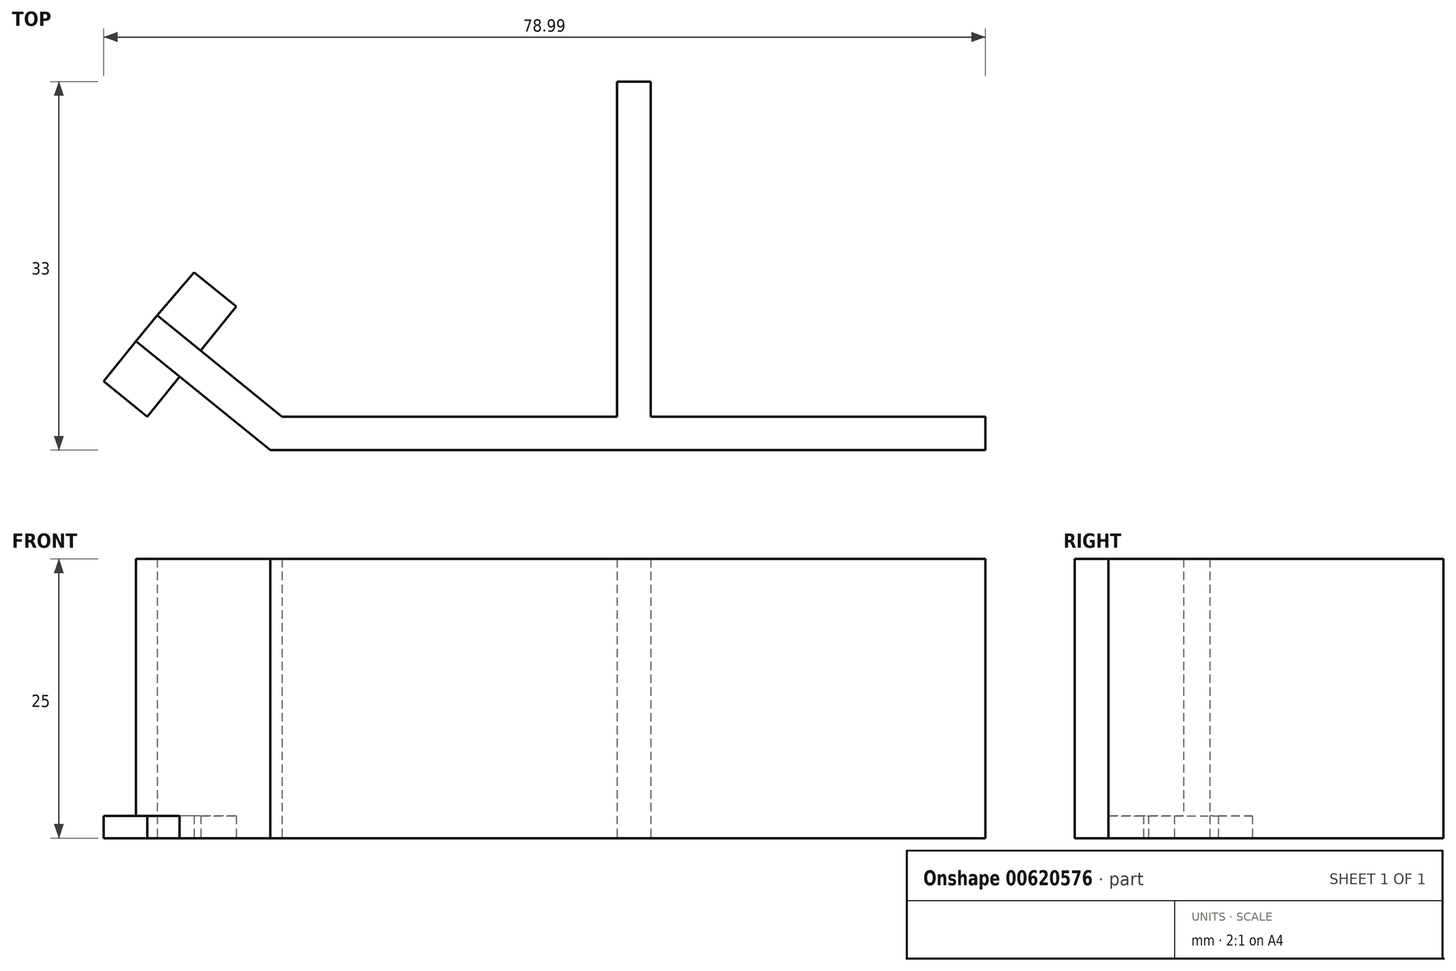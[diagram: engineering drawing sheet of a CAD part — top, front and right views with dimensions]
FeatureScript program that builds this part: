
annotation { "Feature Type Name" : "Feature", "Feature Type Description" : "" }
export const myFeature = defineFeature(function(context is Context, id is Id, definition is map)
    precondition{}
    {
        {
            var Q0;
            Q0=qCreatedBy(makeId("Top.planeOp"),FACE);
            var sketch = newSketch(context, id + "F0", { "sketchPlane" : qUnion([Q0])});
            skLineSegment(sketch, "E0", {"start": v(0, 0) * mm, "end": v(-30, 0) * mm});
            skLineSegment(sketch, "E1", {"start": v(-30, 0) * mm, "end": v(-41.2, 9.08) * mm});
            skLineSegment(sketch, "E2", {"start": v(0, 0) * mm, "end": v(0, 30) * mm});
            skLineSegment(sketch, "E3", {"start": v(3, 30) * mm, "end": v(0, 30) * mm});
            skLineSegment(sketch, "E4", {"start": v(3, 30) * mm, "end": v(3, -3) * mm});
            skLineSegment(sketch, "E5.0", {"start": v(-31.06, -3) * mm, "end": v(-43.08, 6.75) * mm});
            skLineSegment(sketch, "E5.1", {"start": v(3, -3) * mm, "end": v(-31.06, -3) * mm});
            skLineSegment(sketch, "E6", {"start": v(-43.08, 6.75) * mm, "end": v(-41.2, 9.08) * mm});
            skPoint(sketch, "E7.orphan", {"position": v(3, 0) * mm});
            skLineSegment(sketch, "E8", {"start": v(3, -3) * mm, "end": v(33, -3) * mm});
            skLineSegment(sketch, "E9", {"start": v(33, -3) * mm, "end": v(33, 0) * mm});
            skLineSegment(sketch, "E10", {"start": v(33, 0) * mm, "end": v(3, 0) * mm});
            skSolve(sketch);
        }
        {
            var Q0;
            Q0 = qSketchRegion(id + "F0", true);
            extrude(context, id + "F1", {"entities" : qUnion([Q0]), "depth" : 25 * mm, "offsetDistance" : 25 * mm});
        }
        {
            var Q0;
            Q0=makeQuery(id+"F0.imprint","IMPRINT",FACE,{"disambiguationData":[TD([[makeQuery(id+"F0.imprint","IMPRINT",EDGE,{"derivedFrom":sQuery(id+"F0.wireOp",EDGE,"E0")}),1.0]])]});
            var sketch = newSketch(context, id + "F2", { "sketchPlane" : qUnion([Q0])});
            skLineSegment(sketch, "E11.0", {"start": v(-43.08, 6.75) * mm, "end": v(-41.2, 9.08) * mm});
            skLineSegment(sketch, "E12", {"start": v(-43.08, 6.75) * mm, "end": v(-45.99, 3.16) * mm});
            skLineSegment(sketch, "E13", {"start": v(-45.99, 3.16) * mm, "end": v(-42.09, 0) * mm});
            skLineSegment(sketch, "E14", {"start": v(-42.09, 0) * mm, "end": v(-34.1, 9.85) * mm});
            skLineSegment(sketch, "E15", {"start": v(-34.1, 9.85) * mm, "end": v(-37.87, 12.9) * mm});
            skLineSegment(sketch, "E16", {"start": v(-37.87, 12.9) * mm, "end": v(-41.2, 9.08) * mm});
            skSolve(sketch);
        }
        {
            var Q0;
            Q0 = qSketchRegion(id + "F2", true);
            extrude(context, id + "F3", {"entities" : qUnion([Q0]), "operationType" : NewBodyOperationType.ADD, "depth" : 2 * mm, "offsetDistance" : 25 * mm});
        }
    });
